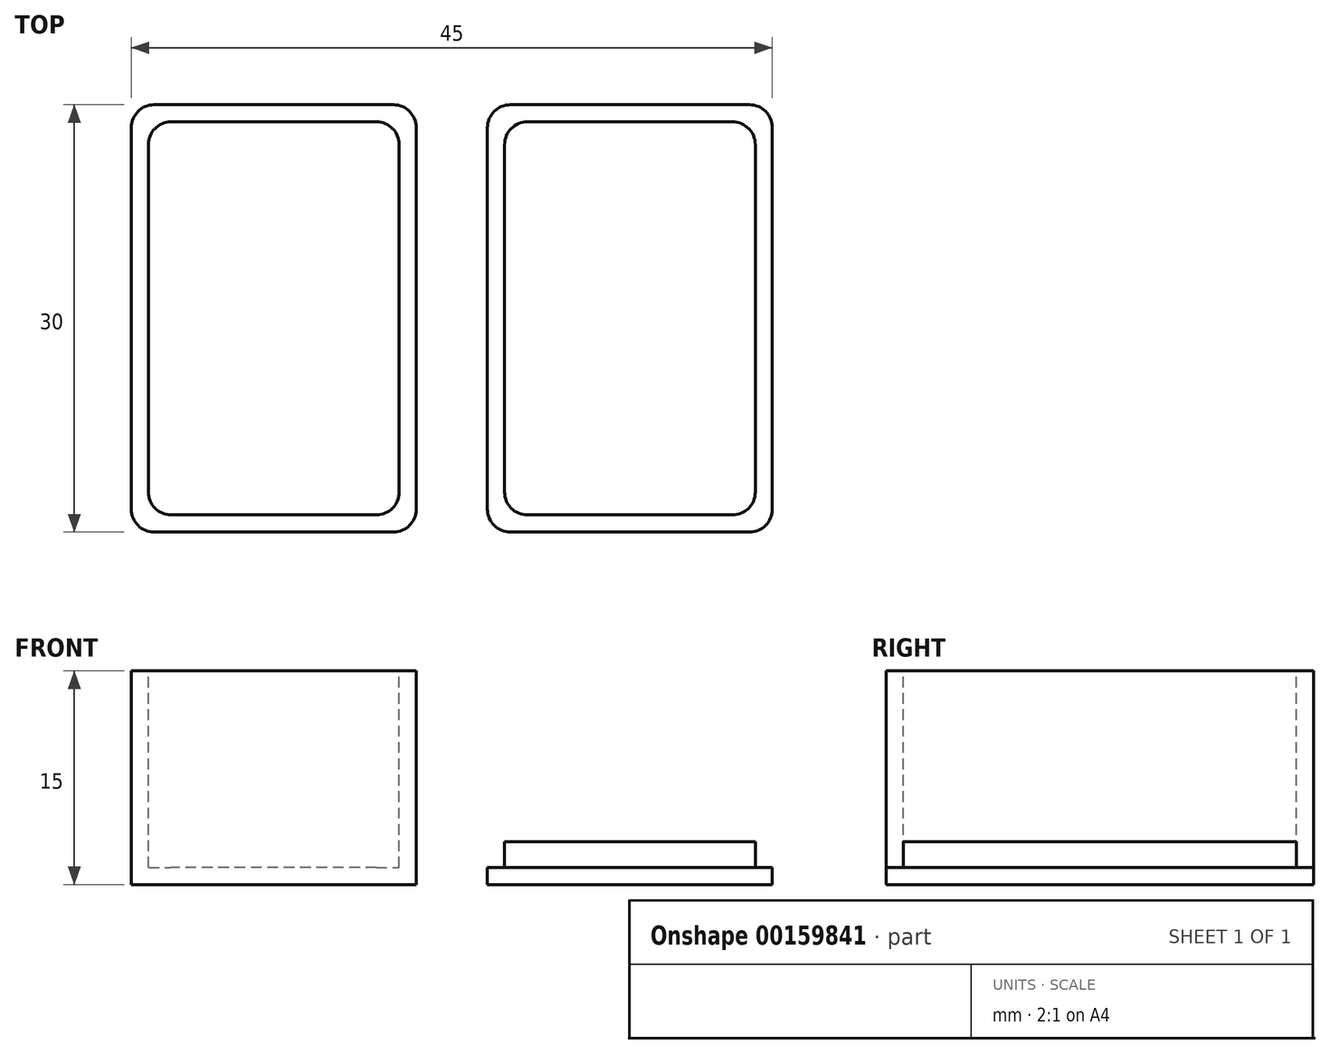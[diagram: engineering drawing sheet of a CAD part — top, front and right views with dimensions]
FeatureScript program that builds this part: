
annotation { "Feature Type Name" : "Feature", "Feature Type Description" : "" }
export const myFeature = defineFeature(function(context is Context, id is Id, definition is map)
    precondition{}
    {
        {
            assignVariable(context, id + "F0", {"name" : "z", "anyValue" : 15 * mm});
        }
        {
            assignVariable(context, id + "F1", {"name" : "ww", "anyValue" : 1.2 * mm});
        }
        {
            assignVariable(context, id + "F2", {"name" : "r", "anyValue" : 1.6});
        }
        {
            assignVariable(context, id + "F3", {"name" : "liddepth", "anyValue" : 1.5 * getVariable(context, 'ww')});
        }
        {
            var Q0;
            Q0=qCreatedBy(makeId("Top.planeOp"),FACE);
            var sketch = newSketch(context, id + "F4", { "sketchPlane" : qUnion([Q0])});
            skLineSegment(sketch, "E0.bottom", {"start": v(10, 15) * mm, "end": v(-10, 15) * mm});
            skLineSegment(sketch, "E0.top", {"start": v(10, -15) * mm, "end": v(-10, -15) * mm});
            skLineSegment(sketch, "E0.left", {"start": v(10, 15) * mm, "end": v(10, -15) * mm});
            skLineSegment(sketch, "E0.right", {"start": v(-10, 15) * mm, "end": v(-10, -15) * mm});
            skPoint(sketch, "E0.middle", {"position": v(0, 0) * mm});
            skSolve(sketch);
        }
        {
            var Q0;
            Q0=qSketchRegion(id+"F4",true);
            extrude(context, id + "F5", {"entities" : qUnion([Q0]), "depth" : getVariable(context, 'z')});
        }
        {
            var Q0;
            Q0=makeQuery(id+"F5.opExtrude","CAP_FACE",FACE,{"disambiguationData":[OSD([sQuery(id+"F4.wireOp",EDGE,"E0.bottom"),sQuery(id+"F4.wireOp",EDGE,"E0.top"),sQuery(id+"F4.wireOp",EDGE,"E0.left"),sQuery(id+"F4.wireOp",EDGE,"E0.right")])],"isStart":false});
            var sketch = newSketch(context, id + "F6", { "sketchPlane" : qUnion([Q0])});
            skLineSegment(sketch, "E1.bottom", {"start": v(8.8, -13.8) * mm, "end": v(-8.8, -13.8) * mm});
            skLineSegment(sketch, "E1.top", {"start": v(8.8, 13.8) * mm, "end": v(-8.8, 13.8) * mm});
            skLineSegment(sketch, "E1.left", {"start": v(8.8, -13.8) * mm, "end": v(8.8, 13.8) * mm});
            skLineSegment(sketch, "E1.right", {"start": v(-8.8, -13.8) * mm, "end": v(-8.8, 13.8) * mm});
            skPoint(sketch, "E1.middle", {"position": v(0, 0) * mm});
            skSolve(sketch);
        }
        {
            var Q0;
            Q0=qSketchRegion(id+"F6",true);
            extrude(context, id + "F7", {"entities" : qUnion([Q0]), "operationType" : NewBodyOperationType.REMOVE, "oppositeDirection" : true, "depth" : getVariable(context, 'z') - getVariable(context, 'ww')});
        }
        {
            var Q0;
            Q0=makeQuery(id+"F5.opExtrude","SWEPT_EDGE",EDGE,{"disambiguationData":[OSD([sQuery(id+"F4.wireOp",EDGE,"E0.bottom"),sQuery(id+"F4.wireOp",EDGE,"E0.left")])]});
            var Q1;
            Q1=makeQuery(id+"F5.opExtrude","SWEPT_EDGE",EDGE,{"disambiguationData":[OSD([sQuery(id+"F4.wireOp",EDGE,"E0.top"),sQuery(id+"F4.wireOp",EDGE,"E0.left")])]});
            var Q2;
            Q2=makeQuery(id+"F5.opExtrude","SWEPT_EDGE",EDGE,{"disambiguationData":[OSD([sQuery(id+"F4.wireOp",EDGE,"E0.top"),sQuery(id+"F4.wireOp",EDGE,"E0.right")])]});
            var Q3;
            Q3=makeQuery(id+"F5.opExtrude","SWEPT_EDGE",EDGE,{"disambiguationData":[OSD([sQuery(id+"F4.wireOp",EDGE,"E0.bottom"),sQuery(id+"F4.wireOp",EDGE,"E0.right")])]});
            var Q4;
            Q4=makeQuery(id+"F7.boolean.opBoolean","COPY",EDGE,{"derivedFrom":makeQuery(id+"F7.opExtrude","SWEPT_EDGE",EDGE,{"disambiguationData":[OSD([sQuery(id+"F6.wireOp",EDGE,"E1.top"),sQuery(id+"F6.wireOp",EDGE,"E1.right")])]})});
            var Q5;
            Q5=makeQuery(id+"F7.boolean.opBoolean","COPY",EDGE,{"derivedFrom":makeQuery(id+"F7.opExtrude","SWEPT_EDGE",EDGE,{"disambiguationData":[OSD([sQuery(id+"F6.wireOp",EDGE,"E1.top"),sQuery(id+"F6.wireOp",EDGE,"E1.left")])]})});
            var Q6;
            Q6=makeQuery(id+"F7.boolean.opBoolean","COPY",EDGE,{"derivedFrom":makeQuery(id+"F7.opExtrude","SWEPT_EDGE",EDGE,{"disambiguationData":[OSD([sQuery(id+"F6.wireOp",EDGE,"E1.bottom"),sQuery(id+"F6.wireOp",EDGE,"E1.left")])]})});
            var Q7;
            Q7=makeQuery(id+"F7.boolean.opBoolean","COPY",EDGE,{"derivedFrom":makeQuery(id+"F7.opExtrude","SWEPT_EDGE",EDGE,{"disambiguationData":[OSD([sQuery(id+"F6.wireOp",EDGE,"E1.bottom"),sQuery(id+"F6.wireOp",EDGE,"E1.right")])]})});
            fillet(context, id + "F8", {"entities" : qUnion([Q0, Q1, Q2, Q3, Q4, Q5, Q6, Q7]), "radius" : (getVariable(context, 'r')) * mm, "tangentPropagation" : true, "allowEdgeOverflow" : false});
        }
        {
            var Q0;
            Q0=qCreatedBy(makeId("Top.planeOp"),FACE);
            var sketch = newSketch(context, id + "F9", { "sketchPlane" : qUnion([Q0])});
            skLineSegment(sketch, "E2.bottom", {"start": v(35, 15) * mm, "end": v(15, 15) * mm});
            skLineSegment(sketch, "E2.top", {"start": v(35, -15) * mm, "end": v(15, -15) * mm});
            skLineSegment(sketch, "E2.left", {"start": v(35, 15) * mm, "end": v(35, -15) * mm});
            skLineSegment(sketch, "E2.right", {"start": v(15, 15) * mm, "end": v(15, -15) * mm});
            skPoint(sketch, "E2.middle", {"position": v(25, 0) * mm});
            skSolve(sketch);
        }
        {
            var Q0;
            Q0=qSketchRegion(id+"F9",true);
            extrude(context, id + "F10", {"entities" : qUnion([Q0]), "depth" : getVariable(context, 'ww')});
        }
        {
            var Q0;
            Q0=makeQuery(id+"F10.opExtrude","CAP_FACE",FACE,{"disambiguationData":[OSD([sQuery(id+"F9.wireOp",EDGE,"E2.bottom"),sQuery(id+"F9.wireOp",EDGE,"E2.top"),sQuery(id+"F9.wireOp",EDGE,"E2.left"),sQuery(id+"F9.wireOp",EDGE,"E2.right")])],"isStart":false});
            var sketch = newSketch(context, id + "F11", { "sketchPlane" : qUnion([Q0])});
            skLineSegment(sketch, "E3.bottom", {"start": v(33.8, 13.8) * mm, "end": v(16.2, 13.8) * mm});
            skLineSegment(sketch, "E3.top", {"start": v(33.8, -13.8) * mm, "end": v(16.2, -13.8) * mm});
            skLineSegment(sketch, "E3.left", {"start": v(33.8, 13.8) * mm, "end": v(33.8, -13.8) * mm});
            skLineSegment(sketch, "E3.right", {"start": v(16.2, 13.8) * mm, "end": v(16.2, -13.8) * mm});
            skPoint(sketch, "E3.middle", {"position": v(25, 0) * mm});
            skPoint(sketch, "E3.middle.positionSnap0", {"position": v(35, 0) * mm});
            skPoint(sketch, "E3.centerSnap0", {"position": v(35, 0) * mm});
            skSolve(sketch);
        }
        {
            var Q0;
            Q0=qSketchRegion(id+"F11",true);
            extrude(context, id + "F12", {"entities" : qUnion([Q0]), "operationType" : NewBodyOperationType.ADD, "depth" : getVariable(context, 'liddepth')});
        }
        {
            var Q0;
            Q0=makeQuery(id+"F10.opExtrude","SWEPT_EDGE",EDGE,{"disambiguationData":[OSD([sQuery(id+"F9.wireOp",EDGE,"E2.bottom"),sQuery(id+"F9.wireOp",EDGE,"E2.left")])]});
            var Q1;
            Q1=makeQuery(id+"F12.opExtrude","SWEPT_EDGE",EDGE,{"disambiguationData":[OSD([sQuery(id+"F11.wireOp",EDGE,"E3.bottom"),sQuery(id+"F11.wireOp",EDGE,"E3.left")])]});
            var Q2;
            Q2=makeQuery(id+"F12.opExtrude","SWEPT_EDGE",EDGE,{"disambiguationData":[OSD([sQuery(id+"F11.wireOp",EDGE,"E3.top"),sQuery(id+"F11.wireOp",EDGE,"E3.left")])]});
            var Q3;
            Q3=makeQuery(id+"F10.opExtrude","SWEPT_EDGE",EDGE,{"disambiguationData":[OSD([sQuery(id+"F9.wireOp",EDGE,"E2.top"),sQuery(id+"F9.wireOp",EDGE,"E2.left")])]});
            var Q4;
            Q4=makeQuery(id+"F12.opExtrude","SWEPT_EDGE",EDGE,{"disambiguationData":[OSD([sQuery(id+"F11.wireOp",EDGE,"E3.top"),sQuery(id+"F11.wireOp",EDGE,"E3.right")])]});
            var Q5;
            Q5=makeQuery(id+"F10.opExtrude","SWEPT_EDGE",EDGE,{"disambiguationData":[OSD([sQuery(id+"F9.wireOp",EDGE,"E2.top"),sQuery(id+"F9.wireOp",EDGE,"E2.right")])]});
            var Q6;
            Q6=makeQuery(id+"F10.opExtrude","SWEPT_EDGE",EDGE,{"disambiguationData":[OSD([sQuery(id+"F9.wireOp",EDGE,"E2.bottom"),sQuery(id+"F9.wireOp",EDGE,"E2.right")])]});
            var Q7;
            Q7=makeQuery(id+"F12.opExtrude","SWEPT_EDGE",EDGE,{"disambiguationData":[OSD([sQuery(id+"F11.wireOp",EDGE,"E3.bottom"),sQuery(id+"F11.wireOp",EDGE,"E3.right")])]});
            fillet(context, id + "F13", {"entities" : qUnion([Q0, Q1, Q2, Q3, Q4, Q5, Q6, Q7]), "radius" : (getVariable(context, 'r')) * mm, "tangentPropagation" : true, "allowEdgeOverflow" : false});
        }
    });
